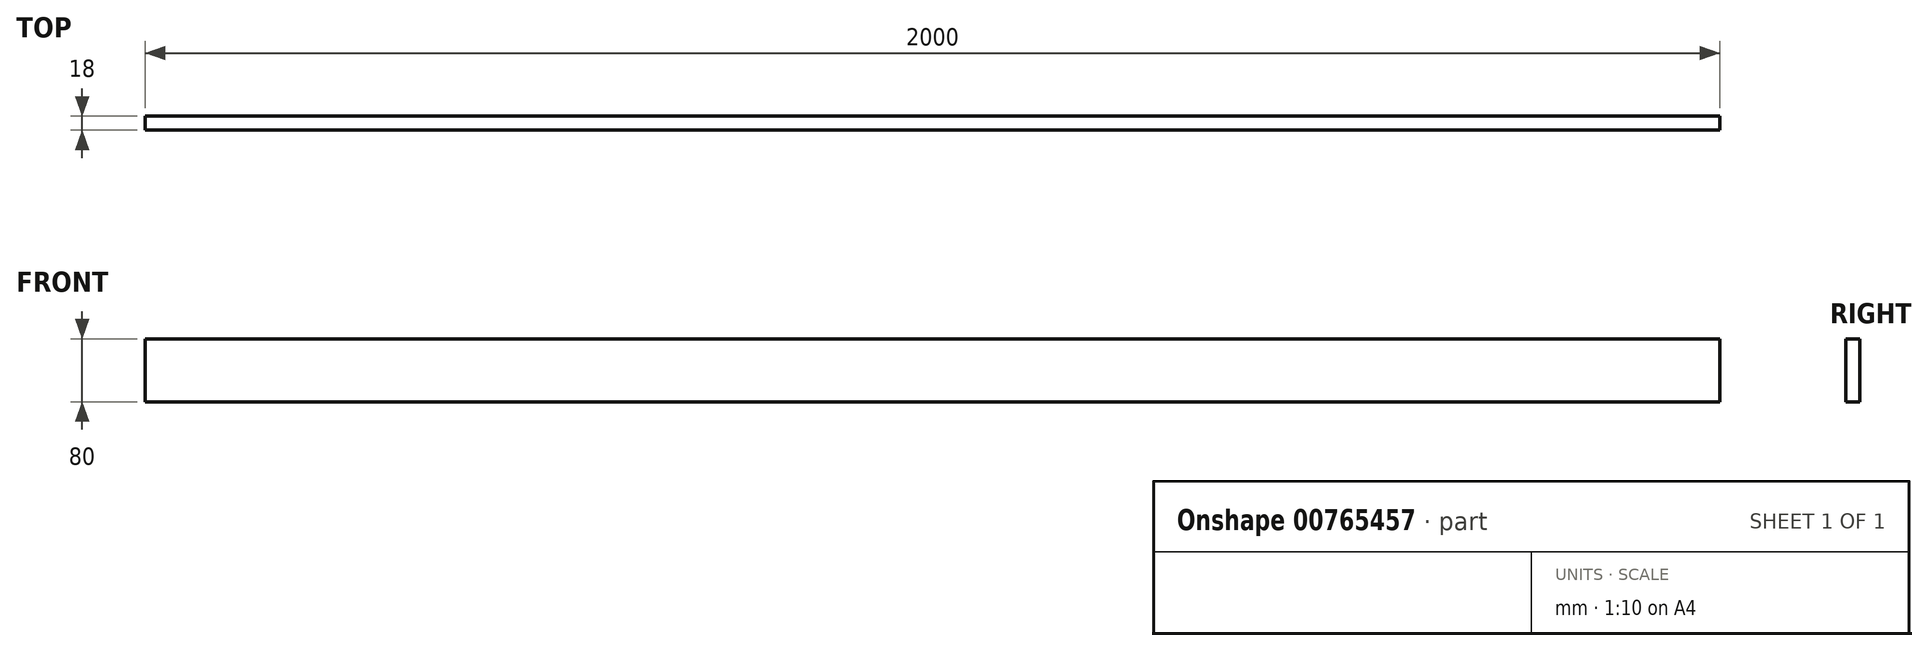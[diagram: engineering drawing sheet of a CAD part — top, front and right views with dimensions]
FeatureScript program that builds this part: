
annotation { "Feature Type Name" : "Feature", "Feature Type Description" : "" }
export const myFeature = defineFeature(function(context is Context, id is Id, definition is map)
    precondition{}
    {
        {
            var Q0;
            Q0=qCreatedBy(makeId("Front.planeOp"),FACE);
            var sketch = newSketch(context, id + "F0", { "sketchPlane" : qUnion([Q0])});
            skLineSegment(sketch, "E0.bottom", {"start": v(-1000, -40) * mm, "end": v(1000, -40) * mm});
            skLineSegment(sketch, "E0.top", {"start": v(-1000, 40) * mm, "end": v(1000, 40) * mm});
            skLineSegment(sketch, "E0.left", {"start": v(-1000, -40) * mm, "end": v(-1000, 40) * mm});
            skLineSegment(sketch, "E0.right", {"start": v(1000, -40) * mm, "end": v(1000, 40) * mm});
            skPoint(sketch, "E0.middle", {"position": v(0, 0) * mm});
            skSolve(sketch);
        }
        {
            var Q0;
            Q0 = qSketchRegion(id + "F0", true);
            extrude(context, id + "F1", {"entities" : qUnion([Q0]), "depth" : 18 * mm, "offsetDistance" : 25 * mm});
        }
    });
